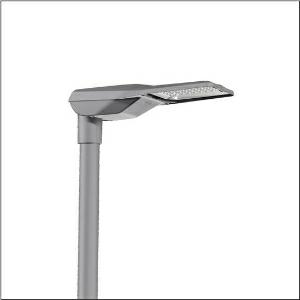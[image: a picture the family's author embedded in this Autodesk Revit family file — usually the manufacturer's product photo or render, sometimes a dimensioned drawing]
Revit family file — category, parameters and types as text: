
# Revit family: streetlight_sl_21_iq_mini___p1_0a_5xe2a41d08hb_633f
name_source: partatom
category: Lighting Fixtures
units: mm (PartAtom-declared; Revit-internal decimal feet)

## family parameters
Cut with Voids When Loaded = No
Host = Face
Light Source = No
Part Type = Normal
Room Calculation Point = No
Round Connector Dimension = Use Diameter
Shared = No

## types (1)
- --- (1 x LED, 9860 lm, 70.9 W, 4000K)
    Apparent Load = 71 VA
    CIE Flux Codes = 21 50 90 100 100
    Color Rendering = 70
    Color Temperature = 4000K
    Default Elevation = 1800 mm
    Description = Streetlight SL 21 iQ mini, mast luminaire, primary light control with lens, of PMMA, primary optical cover: cover, of toughened safety glass, transparent, light distribution: P1.0a, light emission: direct distribution, primary light characteristic: asymmetric, installation type: post-top, side-entry, LED, High Power LED, rated luminous flux: 9.860lm, luminous efficacy: 139lm/W, light colour: 740, colour temperature: 4000K, control gear: iQ-Comfort, control: Auto-Match, Temp-Guard, Lumen-Switch, Night-Set, Smart-Wire, Light-Fading, Desk-Remote (wireless, voltage-free reading and setting of iQ features in the workshop via application-optimized NFC function/RFID function), optimised constant luminous flux control (CLO 2.0), pre-setting: linear dimming characteristic, mains connection: 220..240V, AC, 50/60Hz, start of lifetime: 71W, end of service life: 75W, reduction: 31W, luminaire housing, of diecast aluminium, powder-coated, SITECO metallic grey (DB 702S), corrosivity category C5 high according to DIN EN ISO 12944, please order mast flange separately, inclination adjustable: 0°, 5°, 10°, 15°, sealing non-destructively replaceable, multi-level sealing system, length: 628mm, width: 235mm, height: 110mm, mast flange for spigot size: 42mm (side-entry): 5XC10008XM4, 60/48mm (side-entry/post-top): 5XC10108XM2, 76/60mm (side-entry/post-top): 5XC10108XM1, mounting height: 4..8m, protection rating (complete): IP66, insulation class (complete): insulation class II (safety insulation), certification: CE, ENEC, ENEC+, VDE, impact resistance: IK10, permissible operating ambient temperature for outdoor applications: -40..+50°C, standard-compliant lighting for roads and squares, packaging unit: 1 piece

Light Distribution: P1.0a
    Height = 110 mm
    Lamp = 1 x LED
    Lamp Light Flux = 9860 lm
    Lamp Power = 70.9 W
    Lamp count = 1
    Length = 625 mm
    Luminous efficacy = 139 lm/W
    Manufacturer = Siteco
    ModVariant = No
    Model = 5XE2A41D08HB
    Number of Poles = 1
    OnlyDefault = Yes
    Power Factor = 1
    Product Name = Streetlight SL 21 iQ mini | P1.0a
    Product group = mast luminaire | pylon top
    ProductGroupID = 6100
    Protection Class = Protection class II
    Protection Degree = IP 66
    RLX_Detail_Level = 1
    RLX_Emergency_Light_Flux = 0 lm
    RLX_Emergency_Type = 0
    RLX_Emergency_Type_DB = No
    RlxData = <blob elided: 37529 chars, md5=bd8b98e5>
    Socket = socket
    Standby Power = 0 W
    System Light Flux = 9860 lm
    System Power = 71 W
    Type Comments = factory setting: luminous flux: 100 % | dim-lin: 254 | 711 mA
    Type Image = l_1003519.jpg
    URL = http://relux.com
    VarID = @adj_157109
    Voltage = 0 V
    Weight = 0.00 kg
    Width = 234 mm

## geometry (parser evidence)
native form markers: Blend x4, Sweep x12
no freeform markers — native parametric forms only
